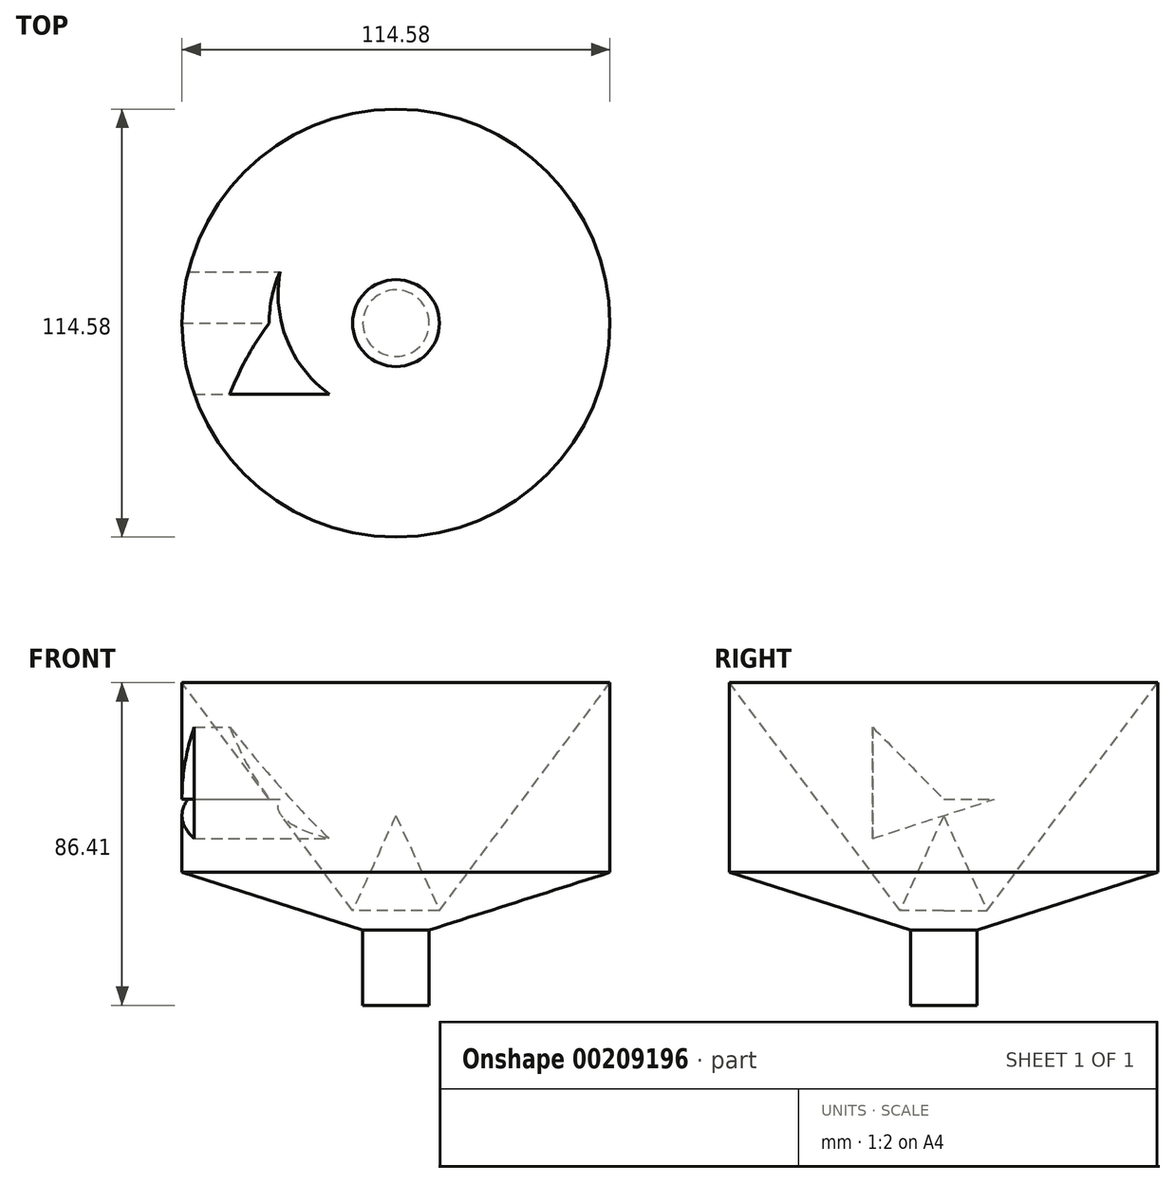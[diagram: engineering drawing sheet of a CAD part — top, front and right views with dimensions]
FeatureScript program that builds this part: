
annotation { "Feature Type Name" : "Feature", "Feature Type Description" : "" }
export const myFeature = defineFeature(function(context is Context, id is Id, definition is map)
    precondition{}
    {
        {
            var Q0;
            Q0=qCreatedBy(makeId("Front.planeOp"),FACE);
            var sketch = newSketch(context, id + "F0", { "sketchPlane" : qUnion([Q0])});
            skLineSegment(sketch, "E0", {"start": v(0, 50.8) * mm, "end": v(0, 0) * mm});
            skLineSegment(sketch, "E1", {"start": v(11.63, 25.4) * mm, "end": v(0, 50.8) * mm});
            skLineSegment(sketch, "E2", {"start": v(11.63, 25.4) * mm, "end": v(57.29, 86.4) * mm});
            skLineSegment(sketch, "E3", {"start": v(57.29, 35.6) * mm, "end": v(57.29, 86.4) * mm});
            skLineSegment(sketch, "E4", {"start": v(0, 0) * mm, "end": v(8.9, 0) * mm});
            skLineSegment(sketch, "E5", {"start": v(8.9, 0) * mm, "end": v(8.9, 20.17) * mm});
            skLineSegment(sketch, "E6", {"start": v(8.9, 20.17) * mm, "end": v(57.29, 35.6) * mm});
            skSolve(sketch);
        }
        {
            var Q0;
            Q0 = qSketchRegion(id + "F0", true);
            var Q1;
            Q1=sQuery(id+"F0.wireOp",EDGE,"E0");
            revolve(context, id + "F1", {"entities" : qUnion([Q0]), "axis" : qUnion([Q1]), "revolveType" : RevolveType.FULL});
        }
        {
            var Q0;
            Q0=qCreatedBy(makeId("Right.planeOp"),FACE);
            var sketch = newSketch(context, id + "F2", { "sketchPlane" : qUnion([Q0])});
            skLineSegment(sketch, "E7", {"start": v(-19, 74.48) * mm, "end": v(-19, 44.68) * mm});
            skLineSegment(sketch, "E8", {"start": v(-19, 44.68) * mm, "end": v(13.66, 55.2) * mm});
            skLineSegment(sketch, "E9", {"start": v(-19, 74.48) * mm, "end": v(0, 55.2) * mm});
            skLineSegment(sketch, "E10", {"start": v(0, 55.2) * mm, "end": v(13.66, 55.2) * mm});
            skSolve(sketch);
        }
        {
            var Q0;
            Q0 = qSketchRegion(id + "F2", true);
            extrude(context, id + "F3", {"entities" : qUnion([Q0]), "operationType" : NewBodyOperationType.REMOVE, "oppositeDirection" : true, "depth" : 160.02 * mm});
        }
    });
